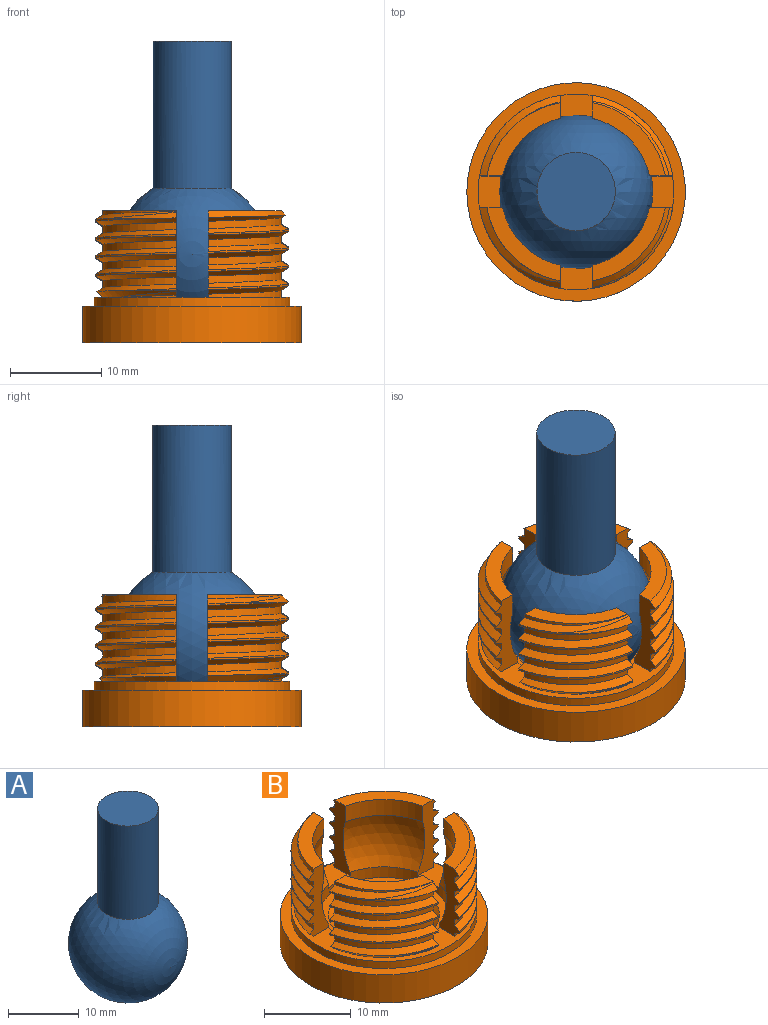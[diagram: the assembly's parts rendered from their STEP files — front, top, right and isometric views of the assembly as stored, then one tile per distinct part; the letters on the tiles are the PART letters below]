
ASSEMBLY  parts=2 mates=1
PART A: 4 faces, bbox 16.8x16.8x31.8 mm
  f0: sphere r=8.42mm, area 775.5mm2, adj f2,f3
  f1: plane 8.6x8.6mm, normal (0,0,1), area 58.1mm2, adj f2
  f2: cylinder r=4.3mm len=16.16mm, axis (0,0,1), area 436.6mm2, adj f0,f1
  f3: plane 7.96x7.96mm, normal (0,0,-1), area 49.8mm2, adj f0
PART B: 112 faces, bbox 24x24.8x15.3 mm
  f0: cylinder r=10.75mm len=8.86mm, axis (0,0,-1), area 2.7mm2, adj f28,f48,f105,f107
  f1: cylinder r=10.75mm len=8.86mm, axis (0,0,-1), area 2.7mm2, adj f27,f47,f105,f107
  f2: cylinder r=10.75mm len=8.86mm, axis (0,0,-1), area 2.7mm2, adj f26,f46,f105,f107
  f3: cylinder r=10.75mm len=8.86mm, axis (0,0,-1), area 2.7mm2, adj f25,f45,f105,f107
  f4: cylinder r=10.75mm len=8.86mm, axis (0,0,-1), area 2.7mm2, adj f33,f52,f103,f104
  f5: cylinder r=10.75mm len=8.86mm, axis (0,0,-1), area 2.7mm2, adj f32,f51,f103,f104
  f6: cylinder r=10.75mm len=8.86mm, axis (0,0,-1), area 2.7mm2, adj f31,f50,f103,f104
  f7: cylinder r=10.75mm len=8.51mm, axis (0,0,-1), area 1.7mm2, adj f23,f30,f49,f104
  f8: cylinder r=10.75mm len=8.86mm, axis (0,0,-1), area 2.7mm2, adj f36,f54,f101,f106
  f9: cylinder r=10.75mm len=8.86mm, axis (0,0,-1), area 2.7mm2, adj f37,f55,f101,f106
  f10: cylinder r=10.75mm len=8.86mm, axis (0,0,-1), area 2.7mm2, adj f38,f56,f101,f106
  f11: cylinder r=10.75mm len=4.63mm, axis (0,0,-1), area 0.4mm2, adj f20,f34,f103
  f12: cylinder r=10.75mm len=8.86mm, axis (0,0,-1), area 2.7mm2, adj f40,f59,f100,f102
  f13: cylinder r=10.75mm len=8.86mm, axis (0,0,-1), area 2.7mm2, adj f41,f60,f100,f102
  f14: cylinder r=10.75mm len=8.86mm, axis (0,0,-1), area 2.7mm2, adj f42,f61,f100,f102
  f15: cylinder r=10.75mm len=8.86mm, axis (0,0,-1), area 2.7mm2, adj f43,f62,f100,f102
  f16: plane 8.05x8.05mm, normal (0,0,1), area 18.3mm2, adj f22,f67,f105,f107,f108
  f17: plane 8.05x8.05mm, normal (0,0,1), area 18.3mm2, adj f72,f103,f104,f110
  f18: plane 8.05x8.05mm, normal (0,0,1), area 18.3mm2, adj f90,f101,f106,f109
  f19: cone r=10.75mm half-angle=45deg, axis (0,0,1), area 8.2mm2, adj f29,f92,f105,f107
  f20: cone r=10.75mm half-angle=45deg, axis (0,0,1), area 9.9mm2, adj f11,f34,f57,f92,f103,f104
  f21: cone r=10.75mm half-angle=45deg, axis (0,0,1), area 2.7mm2, adj f39,f92,f101,f106
  f22: cone r=9.95mm half-angle=45deg, axis (0,0,-1), area 0.3mm2, adj f16,f44,f107
  f23: cone r=9.95mm half-angle=45deg, axis (0,0,-1), area 3.7mm2, adj f7,f30,f49,f103
  f24: cone r=9.95mm half-angle=45deg, axis (0,0,-1), area 10.4mm2, adj f58,f89,f100,f102
  f25: bspline ~16.13x12.41mm, area 12mm2, adj f3,f67,f105,f107
  f26: bspline ~16.13x12.41mm, area 12mm2, adj f2,f66,f105,f107
  f27: bspline ~16.13x12.41mm, area 12mm2, adj f1,f65,f105,f107
  f28: bspline ~16.13x12.41mm, area 12mm2, adj f0,f64,f105,f107
  f29: bspline ~16.13x12.41mm, area 6.8mm2, adj f19,f63,f105,f107
  f30: bspline ~16.13x12.41mm, area 8.9mm2, adj f7,f23,f72,f103,f104
  f31: bspline ~16.13x12.41mm, area 12mm2, adj f6,f71,f103,f104
  f32: bspline ~16.13x12.41mm, area 12mm2, adj f5,f70,f103,f104
  f33: bspline ~16.13x12.41mm, area 12mm2, adj f4,f69,f103,f104
  f34: bspline ~16.13x12.41mm, area 11.3mm2, adj f11,f20,f68,f103,f104
  f35: bspline ~16.13x12.41mm, area 12mm2, adj f73,f88,f101,f106
  f36: bspline ~16.13x12.41mm, area 12mm2, adj f8,f74,f101,f106
  f37: bspline ~16.13x12.41mm, area 12mm2, adj f9,f75,f101,f106
  f38: bspline ~16.13x12.41mm, area 12mm2, adj f10,f76,f101,f106
  f39: bspline ~16.13x12.41mm, area 2.2mm2, adj f21,f77,f101,f106
  f40: bspline ~16.13x12.41mm, area 12mm2, adj f12,f79,f100,f102
  f41: bspline ~16.13x12.41mm, area 12mm2, adj f13,f80,f100,f102
  f42: bspline ~16.13x12.41mm, area 12mm2, adj f14,f81,f100,f102
  f43: bspline ~16.13x12.41mm, area 12mm2, adj f15,f82,f100,f102
  f44: bspline ~16.13x12.41mm, area 0.2mm2, adj f22,f67,f107
  f45: bspline ~16.13x12.41mm, area 12mm2, adj f3,f66,f105,f107
  f46: bspline ~16.13x12.41mm, area 12mm2, adj f2,f65,f105,f107
  f47: bspline ~16.13x12.41mm, area 12mm2, adj f1,f64,f105,f107
  f48: bspline ~16.13x12.41mm, area 12mm2, adj f0,f63,f105,f107
  f49: bspline ~16.13x12.41mm, area 12mm2, adj f7,f23,f71,f103,f104
  f50: bspline ~16.13x12.41mm, area 12mm2, adj f6,f70,f103,f104
  f51: bspline ~16.13x12.41mm, area 12mm2, adj f5,f69,f103,f104
  f52: bspline ~16.13x12.41mm, area 12mm2, adj f4,f68,f103,f104
  f53: bspline ~16.13x12.41mm, area 12mm2, adj f74,f88,f101,f106
  f54: bspline ~16.13x12.41mm, area 12mm2, adj f8,f75,f101,f106
  f55: bspline ~16.13x12.41mm, area 12mm2, adj f9,f76,f101,f106
  f56: bspline ~16.13x12.41mm, area 12mm2, adj f10,f77,f101,f106
  f57: bspline ~16.13x12.41mm, area 3mm2, adj f20,f78,f103
  f58: bspline ~16.13x12.41mm, area 8.6mm2, adj f24,f79,f100,f102
  f59: bspline ~16.13x12.41mm, area 12mm2, adj f12,f80,f100,f102
  f60: bspline ~16.13x12.41mm, area 12mm2, adj f13,f81,f100,f102
  f61: bspline ~16.13x12.41mm, area 12mm2, adj f14,f82,f100,f102
  f62: bspline ~16.13x12.41mm, area 12mm2, adj f15,f83,f100,f102
  f63: cylinder r=9.95mm len=8.05mm, axis (0,0,-1), area 9.7mm2, adj f29,f48,f105,f107
  f64: cylinder r=9.95mm len=8.05mm, axis (0,0,-1), area 9.7mm2, adj f28,f47,f105,f107
  f65: cylinder r=9.95mm len=8.05mm, axis (0,0,-1), area 9.7mm2, adj f27,f46,f105,f107
  f66: cylinder r=9.95mm len=8.05mm, axis (0,0,-1), area 9.7mm2, adj f26,f45,f105,f107
  f67: cylinder r=9.95mm len=8.05mm, axis (0,0,-1), area 8.7mm2, adj f16,f25,f44,f105,f107
  f68: cylinder r=9.95mm len=8.05mm, axis (0,0,-1), area 9.7mm2, adj f34,f52,f103,f104
  f69: cylinder r=9.95mm len=8.05mm, axis (0,0,-1), area 9.7mm2, adj f33,f51,f103,f104
  f70: cylinder r=9.95mm len=8.05mm, axis (0,0,-1), area 9.7mm2, adj f32,f50,f103,f104
  f71: cylinder r=9.95mm len=8.05mm, axis (0,0,-1), area 9.7mm2, adj f31,f49,f103,f104
  f72: cylinder r=9.95mm len=8.05mm, axis (0,0,-1), area 3mm2, adj f17,f30,f103,f104
  f73: cylinder r=9.95mm len=8.05mm, axis (0,0,-1), area 9.7mm2, adj f35,f91,f101,f106
  f74: cylinder r=9.95mm len=8.05mm, axis (0,0,-1), area 9.7mm2, adj f36,f53,f101,f106
  f75: cylinder r=9.95mm len=8.05mm, axis (0,0,-1), area 9.7mm2, adj f37,f54,f101,f106
  f76: cylinder r=9.95mm len=8.05mm, axis (0,0,-1), area 9.7mm2, adj f38,f55,f101,f106
  f77: cylinder r=9.95mm len=8.05mm, axis (0,0,-1), area 9.7mm2, adj f39,f56,f101,f106
  f78: cylinder r=9.95mm len=6.33mm, axis (0,0,-1), area 0.9mm2, adj f57,f92,f103
  f79: cylinder r=9.95mm len=8.05mm, axis (0,0,-1), area 9.7mm2, adj f40,f58,f100,f102
  f80: cylinder r=9.95mm len=8.05mm, axis (0,0,-1), area 9.7mm2, adj f41,f59,f100,f102
  f81: cylinder r=9.95mm len=8.05mm, axis (0,0,-1), area 9.7mm2, adj f42,f60,f100,f102
  f82: cylinder r=9.95mm len=8.05mm, axis (0,0,-1), area 9.7mm2, adj f43,f61,f100,f102
  f83: cylinder r=9.95mm len=8.05mm, axis (0,0,-1), area 6.7mm2, adj f62,f92,f100,f102
  f84: sphere r=8.62mm, area 66.8mm2, adj f87,f105,f107,f108
  f85: sphere r=8.62mm, area 66.8mm2, adj f87,f103,f104,f110
  f86: sphere r=8.62mm, area 66.8mm2, adj f87,f101,f106,f109
  f87: cylinder r=7.5mm len=15mm, axis (0,0,-1), area 63.7mm2, adj f84,f85,f86,f92,f97,f98,f100,f101
  f88: cylinder r=10.75mm len=8.86mm, axis (0,0,-1), area 2.7mm2, adj f35,f53,f101,f106
  f89: plane 8.05x8.05mm, normal (0,0,1), area 18.3mm2, adj f24,f100,f102,f111
  f90: cone r=9.95mm half-angle=45deg, axis (0,0,-1), area 4.9mm2, adj f18,f91,f101,f106
  f91: bspline ~16.13x12.41mm, area 4mm2, adj f73,f90,f101,f106
  f92: plane 21.5x21.5mm, normal (0,0,1), area 86.6mm2, adj f19,f20,f21,f78,f83,f87,f93,f100
  f93: cylinder r=10.75mm len=21.5mm, axis (0,0,1), area 67.5mm2, adj f92,f94
  f94: plane 24x24mm, normal (0,0,1), area 89.3mm2, adj f93,f95
  f95: cylinder r=12mm len=24mm, axis (0,0,1), area 301.6mm2, adj f94,f96
  f96: plane 24x24mm, normal (0,0,-1), area 452.4mm2, adj f95
  f97: sphere r=8.62mm, area 66.8mm2, adj f87,f100,f102,f111
  f98: plane 15x15mm, normal (0,0,1), area 47.1mm2, adj f87,f99
  f99: sphere r=8.62mm, area 155.4mm2, adj f98
  f100: plane 9.51x3.32mm, normal (0,1,0), area 18.6mm2, adj f12,f13,f14,f15,f24,f40,f41,f42
  f101: plane 9.51x3.32mm, normal (0,-1,0), area 18.6mm2, adj f8,f9,f10,f18,f21,f35,f36,f37
  f102: plane 9.51x3.32mm, normal (-1,0,0), area 18.9mm2, adj f12,f13,f14,f15,f24,f40,f41,f42
  f103: plane 9.51x3.32mm, normal (1,0,0), area 18.9mm2, adj f4,f5,f6,f11,f17,f20,f23,f30
  f104: plane 9.51x3.32mm, normal (0,1,0), area 18.8mm2, adj f4,f5,f6,f7,f17,f20,f30,f31
  f105: plane 9.51x3.32mm, normal (0,-1,0), area 18.7mm2, adj f0,f1,f2,f3,f16,f19,f25,f26
  f106: plane 9.51x3.32mm, normal (-1,0,0), area 18.5mm2, adj f8,f9,f10,f18,f21,f35,f36,f37
  f107: plane 9.51x3.32mm, normal (1,0,0), area 18.6mm2, adj f0,f1,f2,f3,f16,f19,f22,f25
  f108: cylinder r=8.25mm len=6.31mm, axis (0,0,1), area 21.2mm2, adj f16,f84,f105,f107
  f109: cylinder r=8.25mm len=6.31mm, axis (0,0,1), area 21.2mm2, adj f18,f86,f101,f106
  f110: cylinder r=8.25mm len=6.31mm, axis (0,0,1), area 21.2mm2, adj f17,f85,f103,f104
  f111: cylinder r=8.25mm len=6.31mm, axis (0,0,1), area 21.2mm2, adj f89,f97,f100,f102
PLACE A t=(-17.27,-5.89,-8.29)mm
PLACE B t=(-17.27,-5.89,-8.29)mm
MATE fastened A.f2 <-> B.f108  axis (0,0,1) through (-17.27,-5.89,-8.29)mm
